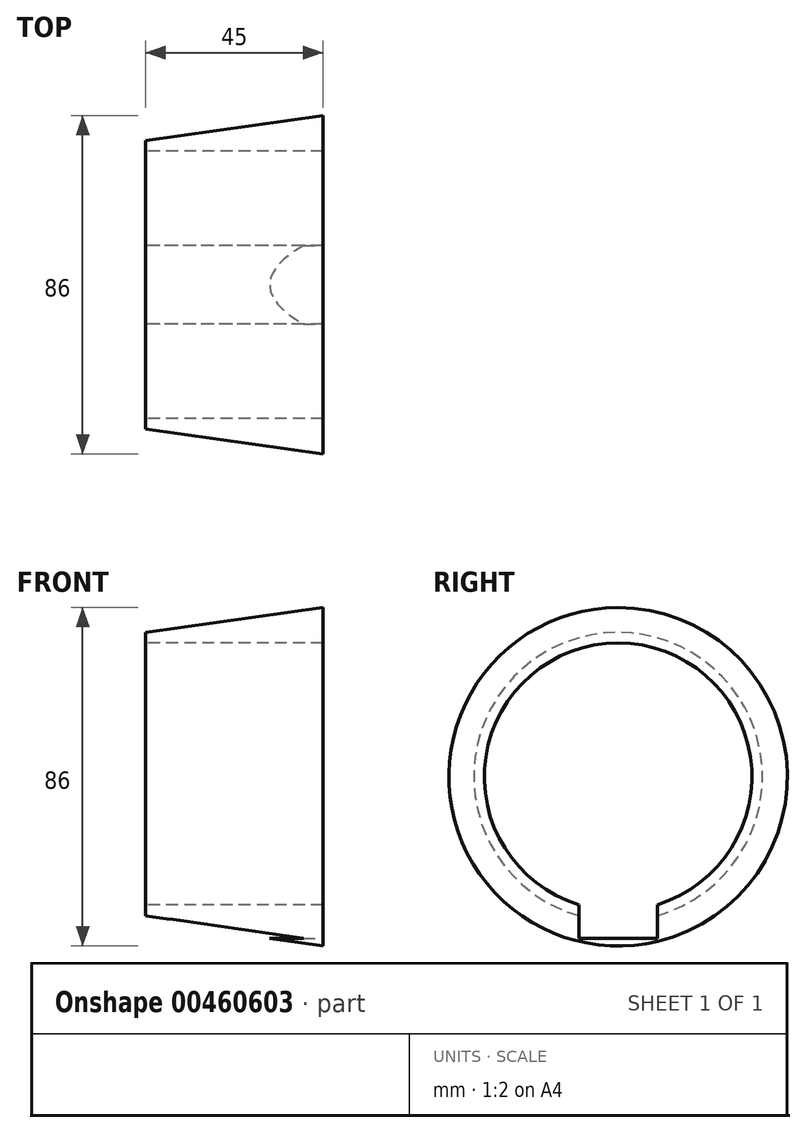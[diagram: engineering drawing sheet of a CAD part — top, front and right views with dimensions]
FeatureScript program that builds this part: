
annotation { "Feature Type Name" : "Feature", "Feature Type Description" : "" }
export const myFeature = defineFeature(function(context is Context, id is Id, definition is map)
    precondition{}
    {
        {
            var Q0;
            Q0=qCreatedBy(makeId("Front.planeOp"),FACE);
            var sketch = newSketch(context, id + "F0", { "sketchPlane" : qUnion([Q0])});
            skLineSegment(sketch, "E0", {"start": v(-22.5, 34) * mm, "end": v(22.5, 34) * mm});
            skLineSegment(sketch, "E1", {"start": v(22.5, 34) * mm, "end": v(22.5, 43) * mm});
            skLineSegment(sketch, "E2", {"start": v(22.5, 43) * mm, "end": v(-22.5, 36.68) * mm});
            skLineSegment(sketch, "E3", {"start": v(-22.5, 36.68) * mm, "end": v(-22.5, 34) * mm});
            skLineSegment(sketch, "E4", {"start": v(-39.96, 0) * mm, "end": v(47.6, 0) * mm, "construction": true});
            skSolve(sketch);
        }
        {
            var Q0;
            Q0 = qSketchRegion(id + "F0", true);
            var Q1;
            Q1=sQuery(id+"F0.wireOp",EDGE,"E4");
            revolve(context, id + "F1", {"entities" : qUnion([Q0]), "axis" : qUnion([Q1]), "revolveType" : RevolveType.FULL});
        }
        {
            var Q0;
            Q0=makeQuery(id+"F1.opRevolve","SWEPT_FACE",FACE,{"disambiguationData":[OSD([sQuery(id+"F0.wireOp",EDGE,"E1")])]});
            var sketch = newSketch(context, id + "F2", { "sketchPlane" : qUnion([Q0])});
            skLineSegment(sketch, "E5.bottom", {"start": v(10, -41.1) * mm, "end": v(-10, -41.1) * mm});
            skLineSegment(sketch, "E5.top", {"start": v(10, -24.5) * mm, "end": v(-10, -24.5) * mm});
            skLineSegment(sketch, "E5.left", {"start": v(10, -41.1) * mm, "end": v(10, -24.5) * mm});
            skLineSegment(sketch, "E5.right", {"start": v(-10, -41.1) * mm, "end": v(-10, -24.5) * mm});
            skCircle(sketch, "E6.0", {"center": v(0, 0) * mm, "radius": 43 * mm, "construction": true});
            skSolve(sketch);
        }
        {
            var Q0;
            Q0 = qSketchRegion(id + "F2", true);
            extrude(context, id + "F3", {"entities" : qUnion([Q0]), "operationType" : NewBodyOperationType.REMOVE, "endBound" : BoundingType.THROUGH_ALL, "oppositeDirection" : true, "depth" : 25 * mm});
        }
    });
